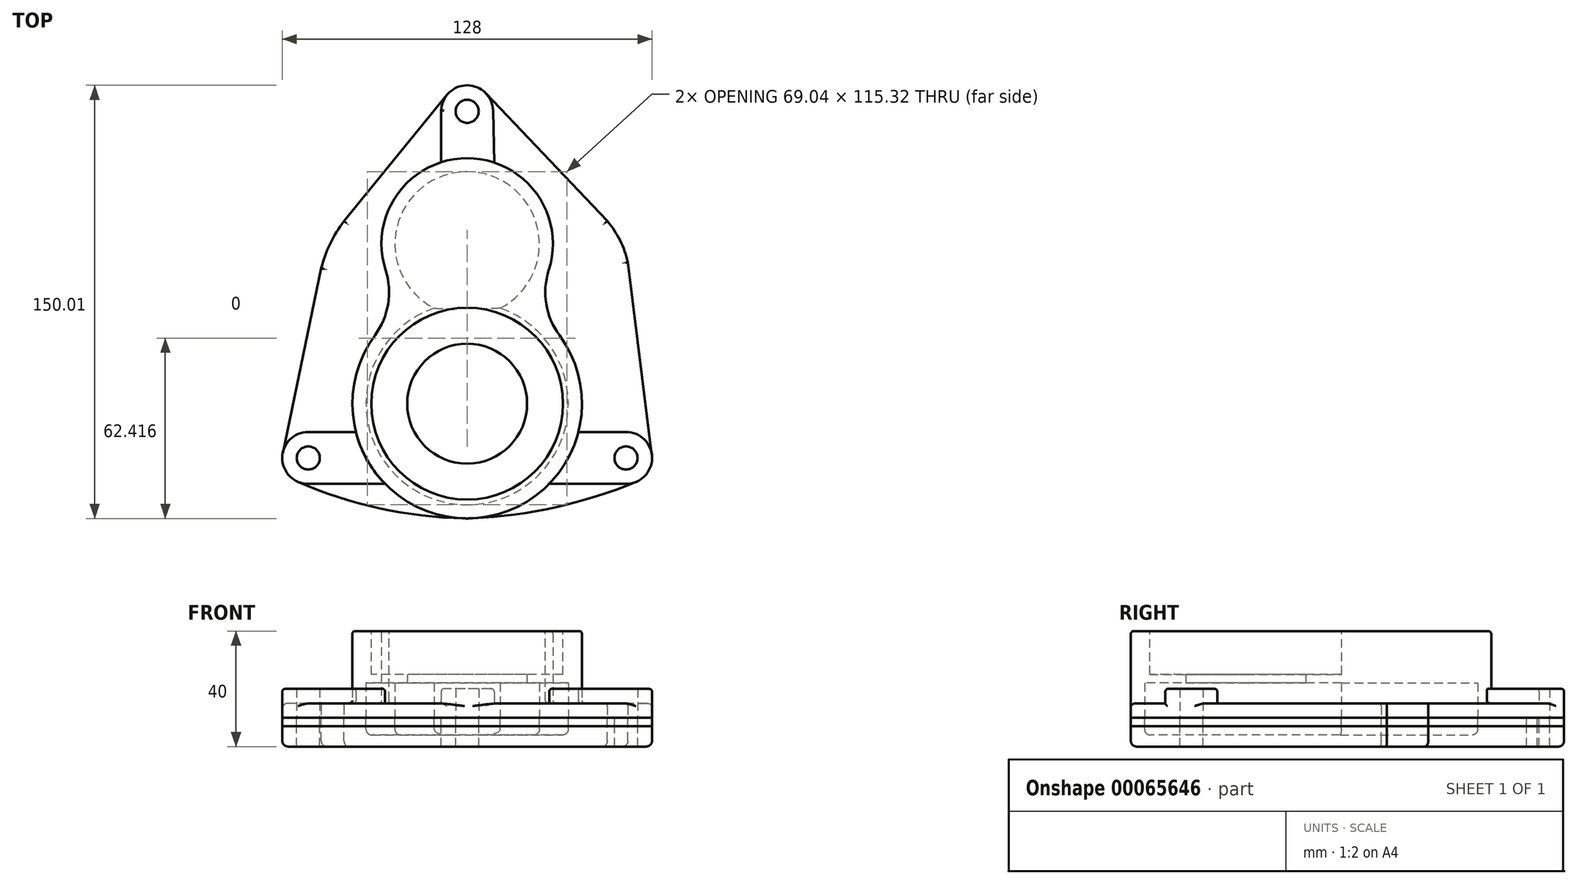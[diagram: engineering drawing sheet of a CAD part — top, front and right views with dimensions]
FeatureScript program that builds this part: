
annotation { "Feature Type Name" : "Feature", "Feature Type Description" : "" }
export const myFeature = defineFeature(function(context is Context, id is Id, definition is map)
    precondition{}
    {
        {
            var Q0;
            Q0=qCreatedBy(makeId("Top.planeOp"),FACE);
            var sketch = newSketch(context, id + "F0", { "sketchPlane" : qUnion([Q0])});
            skCircle(sketch, "E0", {"center": v(0, 23.9) * mm, "radius": 25 * mm});
            skCircle(sketch, "E1", {"center": v(0, -31.42) * mm, "radius": 20.75 * mm});
            skCircle(sketch, "E2", {"center": v(0, -31.42) * mm, "radius": 35 * mm});
            skCircle(sketch, "E3", {"center": v(0, -31.42) * mm, "radius": 39.75 * mm});
            skCircle(sketch, "E4", {"center": v(55, -50.22) * mm, "radius": 9 * mm});
            skCircle(sketch, "E5", {"center": v(-55, -50.22) * mm, "radius": 9 * mm});
            skCircle(sketch, "E6", {"center": v(0, 69.84) * mm, "radius": 9 * mm});
            skCircle(sketch, "E7", {"center": v(0, 69.84) * mm, "radius": 4 * mm});
            skCircle(sketch, "E8", {"center": v(-55, -50.22) * mm, "radius": 4 * mm});
            skCircle(sketch, "E9", {"center": v(55, -50.22) * mm, "radius": 4 * mm});
            skLineSegment(sketch, "E10", {"start": v(0, 23.9) * mm, "end": v(-25, 23.9) * mm, "construction": true});
            skLineSegment(sketch, "E11", {"start": v(0, 23.9) * mm, "end": v(25, 23.9) * mm, "construction": true});
            skLineSegment(sketch, "E12", {"start": v(-42.64, 31.8) * mm, "end": v(-6.97, 75.53) * mm});
            skLineSegment(sketch, "E13", {"start": v(48.5, 31.84) * mm, "end": v(6.53, 76.04) * mm});
            skLineSegment(sketch, "E14", {"start": v(-50.53, 15.5) * mm, "end": v(-63.81, -48.38) * mm});
            skLineSegment(sketch, "E15", {"start": v(55.66, 17.51) * mm, "end": v(63.93, -49.1) * mm});
            skArc(sketch, "E16", {"start": v(-58.6, -58.47) * mm, "mid": v(-30.36, -67.62) * mm, "end": v(-0.9, -71.16) * mm});
            skArc(sketch, "E17", {"start": v(-40.68, 34.2) * mm, "mid": v(-47.63, 23.55) * mm, "end": v(-51.38, 11.39) * mm});
            skArc(sketch, "E18", {"start": v(56.42, 11.39) * mm, "mid": v(54.21, 22.3) * mm, "end": v(48.5, 31.84) * mm});
            skPoint(sketch, "E19.orphan", {"position": v(46.26, 34.2) * mm});
            skPoint(sketch, "E20.end.orphan", {"position": v(0, -50.22) * mm});
            skLineSegment(sketch, "E21", {"start": v(-9, 70.18) * mm, "end": v(-9, 52.19) * mm});
            skLineSegment(sketch, "E22", {"start": v(9, 70.04) * mm, "end": v(9.4, 52.06) * mm});
            skArc(sketch, "E23.trimOffspring", {"start": v(20.62, 2.57) * mm, "mid": v(0.01, 53.6) * mm, "end": v(-20.62, 2.57) * mm});
            skArc(sketch, "E24", {"start": v(1.94, -71.12) * mm, "mid": v(30.72, -67.24) * mm, "end": v(58.42, -58.54) * mm});
            skLineSegment(sketch, "E25", {"start": v(-55, -41.22) * mm, "end": v(-38.53, -41.22) * mm});
            skLineSegment(sketch, "E26", {"start": v(-55, -59.22) * mm, "end": v(-28.41, -59.22) * mm});
            skLineSegment(sketch, "E27", {"start": v(55, -41.22) * mm, "end": v(38.53, -41.22) * mm});
            skLineSegment(sketch, "E28", {"start": v(55, -59.22) * mm, "end": v(28.41, -59.22) * mm});
            skCircle(sketch, "E29", {"center": v(0, -31.42) * mm, "radius": 33.2 * mm});
            skSolve(sketch);
        }
        {
            var Q0;
            {var subQ1=sQuery(id+"F0.wireOp",EDGE,"E3");var subQ3=sQuery(id+"F0.wireOp",EDGE,"E0");var subQ4=makeQuery(id+"F0.imprint","INTERSECT",VERTEX,{"disambiguationData":[OD(0.0)],"derivedFrom":[subQ3,subQ1]});Q0=makeQuery(id+"F0.imprint","IMPRINT",FACE,{"disambiguationData":[TD([[makeQuery(id+"F0.imprint","IMPRINT",EDGE,{"disambiguationData":[TD([[subQ4,1.0]])],"derivedFrom":subQ3}),-1.0]])]});}
            var Q1;
            {var subQ0=sQuery(id+"F0.wireOp",EDGE,"E3");var subQ1=sQuery(id+"F0.wireOp",EDGE,"E0");var subQ2=makeQuery(id+"F0.imprint","INTERSECT",VERTEX,{"disambiguationData":[OD(0.0)],"derivedFrom":[subQ1,subQ0]});Q1=makeQuery(id+"F0.imprint","IMPRINT",FACE,{"disambiguationData":[TD([[makeQuery(id+"F0.imprint","IMPRINT",EDGE,{"disambiguationData":[TD([[subQ2,1.0]])],"derivedFrom":subQ1}),1.0]])]});}
            var Q2;
            {var subQ0=sQuery(id+"F0.wireOp",EDGE,"E2");var subQ1=sQuery(id+"F0.wireOp",EDGE,"E0");var subQ2=makeQuery(id+"F0.imprint","INTERSECT",VERTEX,{"disambiguationData":[OD(0.0)],"derivedFrom":[subQ1,subQ0]});Q2=makeQuery(id+"F0.imprint","IMPRINT",FACE,{"disambiguationData":[TD([[makeQuery(id+"F0.imprint","IMPRINT",EDGE,{"disambiguationData":[TD([[subQ2,1.0]])],"derivedFrom":subQ1}),1.0]])]});}
            var Q3;
            {var subQ0=sQuery(id+"F0.wireOp",EDGE,"E2");var subQ1=sQuery(id+"F0.wireOp",EDGE,"E0");var subQ2=makeQuery(id+"F0.imprint","INTERSECT",VERTEX,{"disambiguationData":[OD(0.0)],"derivedFrom":[subQ1,subQ0]});Q3=makeQuery(id+"F0.imprint","IMPRINT",FACE,{"disambiguationData":[TD([[makeQuery(id+"F0.imprint","IMPRINT",EDGE,{"disambiguationData":[TD([[subQ2,-1.0]])],"derivedFrom":subQ1}),1.0]])]});}
            var Q4;
            {var subQ6=sQuery(id+"F0.wireOp",EDGE,"E2");var subQ7=sQuery(id+"F0.wireOp",EDGE,"E0");var subQ8=makeQuery(id+"F0.imprint","INTERSECT",VERTEX,{"disambiguationData":[OD(0.0)],"derivedFrom":[subQ7,subQ6]});Q4=makeQuery(id+"F0.imprint","IMPRINT",FACE,{"disambiguationData":[TD([[makeQuery(id+"F0.imprint","IMPRINT",EDGE,{"disambiguationData":[TD([[subQ8,1.0]])],"derivedFrom":subQ7}),-1.0]])]});}
            var Q5;
            Q5=makeQuery(id+"F0.imprint","IMPRINT",FACE,{"disambiguationData":[TD([[makeQuery(id+"F0.imprint","IMPRINT",EDGE,{"derivedFrom":sQuery(id+"F0.wireOp",EDGE,"E1")}),-1.0]])]});
            var Q6;
            Q6=makeQuery(id+"F0.imprint","IMPRINT",FACE,{"disambiguationData":[TD([[makeQuery(id+"F0.imprint","IMPRINT",EDGE,{"derivedFrom":sQuery(id+"F0.wireOp",EDGE,"E1")}),1.0]])]});
            var Q7;
            {var subQ0=sQuery(id+"F0.wireOp",EDGE,"E2");var subQ1=sQuery(id+"F0.wireOp",EDGE,"E0");var subQ2=makeQuery(id+"F0.imprint","INTERSECT",VERTEX,{"disambiguationData":[OD(0.0)],"derivedFrom":[subQ1,subQ0]});Q7=makeQuery(id+"F0.imprint","IMPRINT",FACE,{"disambiguationData":[TD([[makeQuery(id+"F0.imprint","IMPRINT",EDGE,{"disambiguationData":[TD([[subQ2,-1.0]])],"derivedFrom":subQ1}),-1.0]])]});}
            var Q8;
            {var subQ0=sQuery(id+"F0.wireOp",EDGE,"E29");var subQ1=sQuery(id+"F0.wireOp",EDGE,"E0");var subQ2=makeQuery(id+"F0.imprint","INTERSECT",VERTEX,{"disambiguationData":[OD(0.0)],"derivedFrom":[subQ1,subQ0]});Q8=makeQuery(id+"F0.imprint","IMPRINT",FACE,{"disambiguationData":[TD([[makeQuery(id+"F0.imprint","IMPRINT",EDGE,{"disambiguationData":[TD([[subQ2,-1.0]])],"derivedFrom":subQ1}),1.0]])]});}
            extrude(context, id + "F1", {"entities" : qUnion([Q0, Q1, Q2, Q3, Q4, Q5, Q6, Q7, Q8]), "depth" : 30 * mm});
        }
        {
            var Q0;
            {var subQ0=sQuery(id+"F0.wireOp",EDGE,"E23.trimOffspring");var subQ1=sQuery(id+"F0.wireOp",EDGE,"E3");Q0=makeQuery(id+"F1.opExtrude","SWEPT_EDGE",EDGE,{"disambiguationData":[OSD([subQ1,subQ0]),TDD([makeQuery(id+"F0.imprint","INTERSECT",VERTEX,{"disambiguationData":[OD(1.0)],"derivedFrom":[subQ1,subQ0]})])]});}
            var Q1;
            {var subQ0=sQuery(id+"F0.wireOp",EDGE,"E23.trimOffspring");var subQ1=sQuery(id+"F0.wireOp",EDGE,"E3");Q1=makeQuery(id+"F1.opExtrude","SWEPT_EDGE",EDGE,{"disambiguationData":[OSD([subQ1,subQ0]),TDD([makeQuery(id+"F0.imprint","INTERSECT",VERTEX,{"disambiguationData":[OD(0.0)],"derivedFrom":[subQ1,subQ0]})])]});}
            fillet(context, id + "F2", {"entities" : qUnion([Q0, Q1]), "radius" : 25 * mm, "tangentPropagation" : true, "allowEdgeOverflow" : false});
        }
        {
            var Q0;
            Q0=makeQuery(id+"F0.imprint","IMPRINT",FACE,{"disambiguationData":[TD([[makeQuery(id+"F0.imprint","IMPRINT",EDGE,{"derivedFrom":sQuery(id+"F0.wireOp",EDGE,"E7")}),-1.0]])]});
            var Q1;
            {var subQ0=sQuery(id+"F0.wireOp",EDGE,"E22");var subQ1=sQuery(id+"F0.wireOp",EDGE,"E6");var subQ2=makeQuery(id+"F0.imprint","INTERSECT",VERTEX,{"derivedFrom":[subQ1,subQ0]});Q1=makeQuery(id+"F0.imprint","IMPRINT",FACE,{"disambiguationData":[TD([[makeQuery(id+"F0.imprint","IMPRINT",EDGE,{"disambiguationData":[TD([[subQ2,1.0]])],"derivedFrom":subQ1}),-1.0]])]});}
            var Q2;
            {var subQ0=sQuery(id+"F0.wireOp",EDGE,"E25");Q2=makeQuery(id+"F0.imprint","IMPRINT",FACE,{"disambiguationData":[TD([[makeQuery(id+"F0.imprint","IMPRINT",EDGE,{"derivedFrom":subQ0}),-1.0]])]});}
            var Q3;
            Q3=makeQuery(id+"F0.imprint","IMPRINT",FACE,{"disambiguationData":[TD([[makeQuery(id+"F0.imprint","IMPRINT",EDGE,{"derivedFrom":sQuery(id+"F0.wireOp",EDGE,"E8")}),-1.0]])]});
            var Q4;
            {var subQ0=sQuery(id+"F0.wireOp",EDGE,"E27");Q4=makeQuery(id+"F0.imprint","IMPRINT",FACE,{"disambiguationData":[TD([[makeQuery(id+"F0.imprint","IMPRINT",EDGE,{"derivedFrom":subQ0}),1.0]])]});}
            var Q5;
            Q5=makeQuery(id+"F0.imprint","IMPRINT",FACE,{"disambiguationData":[TD([[makeQuery(id+"F0.imprint","IMPRINT",EDGE,{"derivedFrom":sQuery(id+"F0.wireOp",EDGE,"E9")}),-1.0]])]});
            extrude(context, id + "F3", {"entities" : qUnion([Q0, Q1, Q2, Q3, Q4, Q5]), "operationType" : NewBodyOperationType.ADD, "depth" : 10 * mm});
        }
        {
            var Q0;
            {var subQ18=sQuery(id+"F0.wireOp",EDGE,"E25");Q0=makeQuery(id+"F0.imprint","IMPRINT",FACE,{"disambiguationData":[TD([[makeQuery(id+"F0.imprint","IMPRINT",EDGE,{"derivedFrom":subQ18}),1.0]])]});}
            var Q1;
            {var subQ0=sQuery(id+"F0.wireOp",EDGE,"E13");Q1=makeQuery(id+"F0.imprint","IMPRINT",FACE,{"disambiguationData":[TD([[makeQuery(id+"F0.imprint","IMPRINT",EDGE,{"derivedFrom":subQ0}),1.0]])]});}
            var Q2;
            {var subQ0=sQuery(id+"F0.wireOp",EDGE,"E24");Q2=makeQuery(id+"F0.imprint","IMPRINT",FACE,{"disambiguationData":[TD([[makeQuery(id+"F0.imprint","IMPRINT",EDGE,{"derivedFrom":subQ0}),1.0]])]});}
            var Q3;
            {var subQ0=sQuery(id+"F0.wireOp",EDGE,"E16");Q3=makeQuery(id+"F0.imprint","IMPRINT",FACE,{"disambiguationData":[TD([[makeQuery(id+"F0.imprint","IMPRINT",EDGE,{"derivedFrom":subQ0}),1.0]])]});}
            extrude(context, id + "F4", {"entities" : qUnion([Q0, Q1, Q2, Q3]), "operationType" : NewBodyOperationType.ADD, "depth" : 5 * mm});
        }
        {
            var Q0;
            {var subQ0=sQuery(id+"F0.wireOp",EDGE,"E3");var subQ1=sQuery(id+"F0.wireOp",EDGE,"E0");var subQ2=makeQuery(id+"F0.imprint","INTERSECT",VERTEX,{"disambiguationData":[OD(0.0)],"derivedFrom":[subQ1,subQ0]});Q0=makeQuery(id+"F0.imprint","IMPRINT",FACE,{"disambiguationData":[TD([[makeQuery(id+"F0.imprint","IMPRINT",EDGE,{"disambiguationData":[TD([[subQ2,1.0]])],"derivedFrom":subQ1}),1.0]])]});}
            var Q1;
            {var subQ0=sQuery(id+"F0.wireOp",EDGE,"E2");var subQ1=sQuery(id+"F0.wireOp",EDGE,"E0");var subQ2=makeQuery(id+"F0.imprint","INTERSECT",VERTEX,{"disambiguationData":[OD(0.0)],"derivedFrom":[subQ1,subQ0]});Q1=makeQuery(id+"F0.imprint","IMPRINT",FACE,{"disambiguationData":[TD([[makeQuery(id+"F0.imprint","IMPRINT",EDGE,{"disambiguationData":[TD([[subQ2,1.0]])],"derivedFrom":subQ1}),1.0]])]});}
            var Q2;
            {var subQ0=sQuery(id+"F0.wireOp",EDGE,"E2");var subQ1=sQuery(id+"F0.wireOp",EDGE,"E0");var subQ2=makeQuery(id+"F0.imprint","INTERSECT",VERTEX,{"disambiguationData":[OD(0.0)],"derivedFrom":[subQ1,subQ0]});Q2=makeQuery(id+"F0.imprint","IMPRINT",FACE,{"disambiguationData":[TD([[makeQuery(id+"F0.imprint","IMPRINT",EDGE,{"disambiguationData":[TD([[subQ2,-1.0]])],"derivedFrom":subQ1}),1.0]])]});}
            var Q3;
            {var subQ0=sQuery(id+"F0.wireOp",EDGE,"E29");var subQ1=sQuery(id+"F0.wireOp",EDGE,"E0");var subQ2=makeQuery(id+"F0.imprint","INTERSECT",VERTEX,{"disambiguationData":[OD(0.0)],"derivedFrom":[subQ1,subQ0]});Q3=makeQuery(id+"F0.imprint","IMPRINT",FACE,{"disambiguationData":[TD([[makeQuery(id+"F0.imprint","IMPRINT",EDGE,{"disambiguationData":[TD([[subQ2,-1.0]])],"derivedFrom":subQ1}),1.0]])]});}
            var Q4;
            Q4=makeQuery(id+"F0.imprint","IMPRINT",FACE,{"disambiguationData":[TD([[makeQuery(id+"F0.imprint","IMPRINT",EDGE,{"derivedFrom":sQuery(id+"F0.wireOp",EDGE,"E1")}),-1.0]])]});
            var Q5;
            Q5=makeQuery(id+"F0.imprint","IMPRINT",FACE,{"disambiguationData":[TD([[makeQuery(id+"F0.imprint","IMPRINT",EDGE,{"derivedFrom":sQuery(id+"F0.wireOp",EDGE,"E1")}),1.0]])]});
            var Q6;
            {var subQ0=sQuery(id+"F0.wireOp",EDGE,"E2");var subQ1=sQuery(id+"F0.wireOp",EDGE,"E0");var subQ2=makeQuery(id+"F0.imprint","INTERSECT",VERTEX,{"disambiguationData":[OD(0.0)],"derivedFrom":[subQ1,subQ0]});Q6=makeQuery(id+"F0.imprint","IMPRINT",FACE,{"disambiguationData":[TD([[makeQuery(id+"F0.imprint","IMPRINT",EDGE,{"disambiguationData":[TD([[subQ2,-1.0]])],"derivedFrom":subQ1}),-1.0]])]});}
            extrude(context, id + "F5", {"entities" : qUnion([Q0, Q1, Q2, Q3, Q4, Q5, Q6]), "operationType" : NewBodyOperationType.REMOVE, "depth" : 12 * mm});
        }
        {
            var Q0;
            Q0=makeQuery(id+"F1.opExtrude","CAP_FACE",FACE,{"disambiguationData":[OSD([sQuery(id+"F0.wireOp",EDGE,"E3"),sQuery(id+"F0.wireOp",EDGE,"E23.trimOffspring")])],"isStart":false});
            var sketch = newSketch(context, id + "F6", { "sketchPlane" : qUnion([Q0])});
            skCircle(sketch, "E30.0", {"center": v(0, -31.42) * mm, "radius": 33.2 * mm});
            skCircle(sketch, "E31.0", {"center": v(0, 23.9) * mm, "radius": 25 * mm});
            skSolve(sketch);
        }
        {
            var Q0;
            Q0=makeQuery(id+"F6.imprint","IMPRINT",FACE,{"disambiguationData":[TD([[makeQuery(id+"F6.imprint","IMPRINT",EDGE,{"derivedFrom":sQuery(id+"F6.wireOp",EDGE,"E30.0")}),1.0]])]});
            extrude(context, id + "F7", {"entities" : qUnion([Q0]), "operationType" : NewBodyOperationType.REMOVE, "oppositeDirection" : true, "depth" : 15 * mm});
        }
        {
            var Q0;
            Q0=makeQuery(id+"F0.imprint","IMPRINT",FACE,{"disambiguationData":[TD([[makeQuery(id+"F0.imprint","IMPRINT",EDGE,{"derivedFrom":sQuery(id+"F0.wireOp",EDGE,"E1")}),1.0]])]});
            extrude(context, id + "F8", {"entities" : qUnion([Q0]), "operationType" : NewBodyOperationType.REMOVE, "endBound" : BoundingType.THROUGH_ALL, "depth" : 25 * mm});
        }
        {
            var Q0;
            Q0=makeQuery(id+"F1.opExtrude","CAP_EDGE",EDGE,{"disambiguationData":[OSD([sQuery(id+"F0.wireOp",EDGE,"E3")])],"isStart":false});
            var Q1;
            {var subQ0=sQuery(id+"F0.wireOp",EDGE,"E23.trimOffspring");var subQ1=sQuery(id+"F0.wireOp",EDGE,"E3");Q1=makeQuery(id+"F2.opFillet","BLEND_EDGE",EDGE,{"blendedFrom":[makeQuery(id+"F1.opExtrude","SWEPT_EDGE",EDGE,{"disambiguationData":[OSD([subQ1,subQ0]),TDD([makeQuery(id+"F0.imprint","INTERSECT",VERTEX,{"disambiguationData":[OD(0.0)],"derivedFrom":[subQ1,subQ0]})])]}),makeQuery(id+"F1.opExtrude","CAP_FACE",FACE,{"disambiguationData":[OSD([subQ1,subQ0])],"isStart":false})],"blendedInto":[makeQuery(id+"F1.opExtrude","CAP_FACE",FACE,{"disambiguationData":[OSD([subQ1,subQ0])],"isStart":false})]});}
            var Q2;
            Q2=makeQuery(id+"F1.opExtrude","CAP_EDGE",EDGE,{"disambiguationData":[OSD([sQuery(id+"F0.wireOp",EDGE,"E23.trimOffspring")])],"isStart":false});
            var Q3;
            {var subQ0=sQuery(id+"F0.wireOp",EDGE,"E23.trimOffspring");var subQ1=sQuery(id+"F0.wireOp",EDGE,"E3");Q3=makeQuery(id+"F4.boolean.opBoolean","INTERSECT",EDGE,{"derivedFrom":[makeQuery(id+"F2.opFillet","BLEND_FACE",FACE,{"disambiguationData":[OSD([subQ1,subQ0]),TDD([makeQuery(id+"F1.opExtrude","SWEPT_EDGE",EDGE,{"disambiguationData":[OSD([subQ1,subQ0]),TDD([makeQuery(id+"F0.imprint","INTERSECT",VERTEX,{"disambiguationData":[OD(0.0)],"derivedFrom":[subQ1,subQ0]})])]})])]}),makeQuery(id+"F4.opExtrude","CAP_FACE",FACE,{"disambiguationData":[OSD([subQ1,sQuery(id+"F0.wireOp",EDGE,"E4"),sQuery(id+"F0.wireOp",EDGE,"E6"),sQuery(id+"F0.wireOp",EDGE,"E13"),sQuery(id+"F0.wireOp",EDGE,"E15"),sQuery(id+"F0.wireOp",EDGE,"E18"),sQuery(id+"F0.wireOp",EDGE,"E22"),subQ0,sQuery(id+"F0.wireOp",EDGE,"E27")])],"isStart":false})]});}
            var Q4;
            {var subQ0=sQuery(id+"F0.wireOp",EDGE,"E3");Q4=makeQuery(id+"F4.opExtrude","CAP_EDGE",EDGE,{"disambiguationData":[OSD([subQ0]),TDD([makeQuery(id+"F0.imprint","IMPRINT",EDGE,{"disambiguationData":[TD([[makeQuery(id+"F0.imprint","INTERSECT",VERTEX,{"derivedFrom":[subQ0,sQuery(id+"F0.wireOp",EDGE,"E24")]}),-1.0]])],"derivedFrom":subQ0})])],"isStart":false});}
            var Q5;
            Q5=makeQuery(id+"F3.opExtrude","SWEPT_EDGE",EDGE,{"disambiguationData":[OSD([sQuery(id+"F0.wireOp",EDGE,"E3"),sQuery(id+"F0.wireOp",EDGE,"E28")])]});
            var Q6;
            {var subQ0=sQuery(id+"F0.wireOp",EDGE,"E3");Q6=makeQuery(id+"F3.opExtrude","CAP_EDGE",EDGE,{"disambiguationData":[OSD([subQ0]),TDD([makeQuery(id+"F0.imprint","IMPRINT",EDGE,{"disambiguationData":[TD([[makeQuery(id+"F0.imprint","INTERSECT",VERTEX,{"derivedFrom":[subQ0,sQuery(id+"F0.wireOp",EDGE,"E27")]}),1.0]])],"derivedFrom":subQ0})])],"isStart":false});}
            var Q7;
            Q7=makeQuery(id+"F3.opExtrude","CAP_EDGE",EDGE,{"disambiguationData":[OSD([sQuery(id+"F0.wireOp",EDGE,"E28")])],"isStart":false});
            var Q8;
            Q8=makeQuery(id+"F4.opExtrude","CAP_EDGE",EDGE,{"disambiguationData":[OSD([sQuery(id+"F0.wireOp",EDGE,"E28")])],"isStart":false});
            var Q9;
            Q9=makeQuery(id+"F4.opExtrude","CAP_EDGE",EDGE,{"disambiguationData":[OSD([sQuery(id+"F0.wireOp",EDGE,"E24")])],"isStart":false});
            var Q10;
            Q10=makeQuery(id+"F4.opExtrude","CAP_EDGE",EDGE,{"disambiguationData":[OSD([sQuery(id+"F0.wireOp",EDGE,"E15")])],"isStart":false});
            var Q11;
            Q11=makeQuery(id+"F4.opExtrude","CAP_EDGE",EDGE,{"disambiguationData":[OSD([sQuery(id+"F0.wireOp",EDGE,"E18")])],"isStart":false});
            var Q12;
            Q12=makeQuery(id+"F3.opExtrude","CAP_EDGE",EDGE,{"disambiguationData":[OSD([sQuery(id+"F0.wireOp",EDGE,"E22")])],"isStart":false});
            var Q13;
            Q13=makeQuery(id+"F3.opExtrude","CAP_EDGE",EDGE,{"disambiguationData":[OSD([sQuery(id+"F0.wireOp",EDGE,"E23.trimOffspring")])],"isStart":false});
            var Q14;
            {var subQ0=sQuery(id+"F0.wireOp",EDGE,"E23.trimOffspring");Q14=makeQuery(id+"F4.opExtrude","CAP_EDGE",EDGE,{"disambiguationData":[OSD([subQ0]),TDD([makeQuery(id+"F0.imprint","IMPRINT",EDGE,{"disambiguationData":[TD([[makeQuery(id+"F0.imprint","INTERSECT",VERTEX,{"disambiguationData":[OD(0.0)],"derivedFrom":[sQuery(id+"F0.wireOp",EDGE,"E3"),subQ0]}),-1.0]])],"derivedFrom":subQ0})])],"isStart":false});}
            var Q15;
            {var subQ0=sQuery(id+"F0.wireOp",EDGE,"E3");Q15=makeQuery(id+"F4.opExtrude","CAP_EDGE",EDGE,{"disambiguationData":[OSD([subQ0]),TDD([makeQuery(id+"F0.imprint","IMPRINT",EDGE,{"disambiguationData":[TD([[makeQuery(id+"F0.imprint","INTERSECT",VERTEX,{"disambiguationData":[OD(0.0)],"derivedFrom":[subQ0,sQuery(id+"F0.wireOp",EDGE,"E23.trimOffspring")]}),1.0]])],"derivedFrom":subQ0})])],"isStart":false});}
            var Q16;
            Q16=makeQuery(id+"F3.opExtrude","SWEPT_EDGE",EDGE,{"disambiguationData":[OSD([sQuery(id+"F0.wireOp",EDGE,"E3"),sQuery(id+"F0.wireOp",EDGE,"E27")])]});
            var Q17;
            Q17=makeQuery(id+"F4.opExtrude","CAP_EDGE",EDGE,{"disambiguationData":[OSD([sQuery(id+"F0.wireOp",EDGE,"E27")])],"isStart":false});
            var Q18;
            Q18=makeQuery(id+"F3.opExtrude","CAP_EDGE",EDGE,{"disambiguationData":[OSD([sQuery(id+"F0.wireOp",EDGE,"E27")])],"isStart":false});
            var Q19;
            Q19=makeQuery(id+"F3.opExtrude","CAP_EDGE",EDGE,{"disambiguationData":[OSD([sQuery(id+"F0.wireOp",EDGE,"E4")])],"isStart":false});
            var Q20;
            {var subQ0=sQuery(id+"F0.wireOp",EDGE,"E4");Q20=makeQuery(id+"F4.opExtrude","CAP_EDGE",EDGE,{"disambiguationData":[OSD([subQ0]),TDD([makeQuery(id+"F0.imprint","IMPRINT",EDGE,{"disambiguationData":[TD([[makeQuery(id+"F0.imprint","INTERSECT",VERTEX,{"derivedFrom":[subQ0,sQuery(id+"F0.wireOp",EDGE,"E15")]}),-1.0]])],"derivedFrom":subQ0})])],"isStart":false});}
            var Q21;
            Q21=makeQuery(id+"F4.opExtrude","CAP_EDGE",EDGE,{"disambiguationData":[OSD([sQuery(id+"F0.wireOp",EDGE,"E13")])],"isStart":false});
            var Q22;
            Q22=makeQuery(id+"F3.opExtrude","CAP_EDGE",EDGE,{"disambiguationData":[OSD([sQuery(id+"F0.wireOp",EDGE,"E6")])],"isStart":false});
            var Q23;
            Q23=makeQuery(id+"F3.opExtrude","CAP_EDGE",EDGE,{"disambiguationData":[OSD([sQuery(id+"F0.wireOp",EDGE,"E21")])],"isStart":false});
            var Q24;
            {var subQ0=sQuery(id+"F0.wireOp",EDGE,"E23.trimOffspring");Q24=makeQuery(id+"F4.opExtrude","CAP_EDGE",EDGE,{"disambiguationData":[OSD([subQ0]),TDD([makeQuery(id+"F0.imprint","IMPRINT",EDGE,{"disambiguationData":[TD([[makeQuery(id+"F0.imprint","INTERSECT",VERTEX,{"disambiguationData":[OD(1.0)],"derivedFrom":[sQuery(id+"F0.wireOp",EDGE,"E3"),subQ0]}),1.0]])],"derivedFrom":subQ0})])],"isStart":false});}
            var Q25;
            {var subQ0=sQuery(id+"F0.wireOp",EDGE,"E23.trimOffspring");var subQ1=sQuery(id+"F0.wireOp",EDGE,"E3");Q25=makeQuery(id+"F4.boolean.opBoolean","INTERSECT",EDGE,{"derivedFrom":[makeQuery(id+"F2.opFillet","BLEND_FACE",FACE,{"disambiguationData":[OSD([subQ1,subQ0]),TDD([makeQuery(id+"F1.opExtrude","SWEPT_EDGE",EDGE,{"disambiguationData":[OSD([subQ1,subQ0]),TDD([makeQuery(id+"F0.imprint","INTERSECT",VERTEX,{"disambiguationData":[OD(1.0)],"derivedFrom":[subQ1,subQ0]})])]})])]}),makeQuery(id+"F4.opExtrude","CAP_FACE",FACE,{"disambiguationData":[OSD([subQ1,sQuery(id+"F0.wireOp",EDGE,"E5"),sQuery(id+"F0.wireOp",EDGE,"E6"),sQuery(id+"F0.wireOp",EDGE,"E12"),sQuery(id+"F0.wireOp",EDGE,"E14"),sQuery(id+"F0.wireOp",EDGE,"E17"),sQuery(id+"F0.wireOp",EDGE,"E21"),subQ0,sQuery(id+"F0.wireOp",EDGE,"E25")])],"isStart":false})]});}
            var Q26;
            Q26=makeQuery(id+"F4.opExtrude","CAP_EDGE",EDGE,{"disambiguationData":[OSD([sQuery(id+"F0.wireOp",EDGE,"E17")])],"isStart":false});
            var Q27;
            {var subQ0=sQuery(id+"F0.wireOp",EDGE,"E21");var subQ1=sQuery(id+"F0.wireOp",EDGE,"E6");var subQ2=makeQuery(id+"F0.imprint","INTERSECT",VERTEX,{"disambiguationData":[OD(0.0)],"derivedFrom":[subQ1,subQ0]});Q27=makeQuery(id+"F4.boolean.opBoolean","MERGE",EDGE,{"derivedFrom":[makeQuery(id+"F4.opExtrude","CAP_EDGE",EDGE,{"disambiguationData":[OSD([subQ1]),TDD([makeQuery(id+"F0.imprint","IMPRINT",EDGE,{"disambiguationData":[TD([[makeQuery(id+"F0.imprint","INTERSECT",VERTEX,{"derivedFrom":[subQ1,sQuery(id+"F0.wireOp",EDGE,"E12")]}),-1.0]])],"derivedFrom":subQ1}),makeQuery(id+"F0.imprint","IMPRINT",EDGE,{"disambiguationData":[TD([[subQ2,-1.0]])],"derivedFrom":subQ1})])],"isStart":false}),makeQuery(id+"F4.opExtrude","CAP_EDGE",EDGE,{"disambiguationData":[OSD([subQ0])],"isStart":false})]});}
            var Q28;
            {var subQ0=sQuery(id+"F0.wireOp",EDGE,"E21");var subQ1=sQuery(id+"F0.wireOp",EDGE,"E6");var subQ2=makeQuery(id+"F0.imprint","INTERSECT",VERTEX,{"disambiguationData":[OD(0.0)],"derivedFrom":[subQ1,subQ0]});Q28=makeQuery(id+"F4.boolean.opBoolean","SPLIT",EDGE,{"derivedFrom":makeQuery(id+"F4.opExtrude","CAP_EDGE",EDGE,{"disambiguationData":[OSD([subQ1]),TDD([makeQuery(id+"F0.imprint","IMPRINT",EDGE,{"disambiguationData":[TD([[makeQuery(id+"F0.imprint","INTERSECT",VERTEX,{"derivedFrom":[subQ1,sQuery(id+"F0.wireOp",EDGE,"E12")]}),-1.0]])],"derivedFrom":subQ1}),makeQuery(id+"F0.imprint","IMPRINT",EDGE,{"disambiguationData":[TD([[subQ2,-1.0]])],"derivedFrom":subQ1})])],"isStart":false})});}
            var Q29;
            Q29=makeQuery(id+"F4.opExtrude","CAP_EDGE",EDGE,{"disambiguationData":[OSD([sQuery(id+"F0.wireOp",EDGE,"E12")])],"isStart":false});
            var Q30;
            Q30=makeQuery(id+"F4.opExtrude","CAP_EDGE",EDGE,{"disambiguationData":[OSD([sQuery(id+"F0.wireOp",EDGE,"E25")])],"isStart":false});
            var Q31;
            {var subQ0=sQuery(id+"F0.wireOp",EDGE,"E5");Q31=makeQuery(id+"F4.opExtrude","CAP_EDGE",EDGE,{"disambiguationData":[OSD([subQ0]),TDD([makeQuery(id+"F0.imprint","IMPRINT",EDGE,{"disambiguationData":[TD([[makeQuery(id+"F0.imprint","INTERSECT",VERTEX,{"derivedFrom":[subQ0,sQuery(id+"F0.wireOp",EDGE,"E14")]}),1.0]])],"derivedFrom":subQ0})])],"isStart":false});}
            var Q32;
            Q32=makeQuery(id+"F4.opExtrude","CAP_EDGE",EDGE,{"disambiguationData":[OSD([sQuery(id+"F0.wireOp",EDGE,"E14")])],"isStart":false});
            var Q33;
            Q33=makeQuery(id+"F3.opExtrude","CAP_EDGE",EDGE,{"disambiguationData":[OSD([sQuery(id+"F0.wireOp",EDGE,"E25")])],"isStart":false});
            var Q34;
            {var subQ0=sQuery(id+"F0.wireOp",EDGE,"E3");Q34=makeQuery(id+"F3.opExtrude","CAP_EDGE",EDGE,{"disambiguationData":[OSD([subQ0]),TDD([makeQuery(id+"F0.imprint","IMPRINT",EDGE,{"disambiguationData":[TD([[makeQuery(id+"F0.imprint","INTERSECT",VERTEX,{"derivedFrom":[subQ0,sQuery(id+"F0.wireOp",EDGE,"E25")]}),-1.0]])],"derivedFrom":subQ0})])],"isStart":false});}
            var Q35;
            {var subQ0=sQuery(id+"F0.wireOp",EDGE,"E23.trimOffspring");var subQ1=sQuery(id+"F0.wireOp",EDGE,"E3");Q35=makeQuery(id+"F2.opFillet","BLEND_EDGE",EDGE,{"blendedFrom":[makeQuery(id+"F1.opExtrude","SWEPT_EDGE",EDGE,{"disambiguationData":[OSD([subQ1,subQ0]),TDD([makeQuery(id+"F0.imprint","INTERSECT",VERTEX,{"disambiguationData":[OD(1.0)],"derivedFrom":[subQ1,subQ0]})])]}),makeQuery(id+"F1.opExtrude","CAP_FACE",FACE,{"disambiguationData":[OSD([subQ1,subQ0])],"isStart":false})],"blendedInto":[makeQuery(id+"F1.opExtrude","CAP_FACE",FACE,{"disambiguationData":[OSD([subQ1,subQ0])],"isStart":false})]});}
            var Q36;
            Q36=makeQuery(id+"F4.opExtrude","CAP_EDGE",EDGE,{"disambiguationData":[OSD([sQuery(id+"F0.wireOp",EDGE,"E26")])],"isStart":false});
            var Q37;
            Q37=makeQuery(id+"F4.opExtrude","CAP_EDGE",EDGE,{"disambiguationData":[OSD([sQuery(id+"F0.wireOp",EDGE,"E16")])],"isStart":false});
            var Q38;
            {var subQ0=sQuery(id+"F0.wireOp",EDGE,"E3");Q38=makeQuery(id+"F4.opExtrude","CAP_EDGE",EDGE,{"disambiguationData":[OSD([subQ0]),TDD([makeQuery(id+"F0.imprint","IMPRINT",EDGE,{"disambiguationData":[TD([[makeQuery(id+"F0.imprint","INTERSECT",VERTEX,{"derivedFrom":[subQ0,sQuery(id+"F0.wireOp",EDGE,"E16")]}),1.0]])],"derivedFrom":subQ0})])],"isStart":false});}
            fillet(context, id + "F9", {"entities" : qUnion([Q0, Q1, Q2, Q3, Q4, Q5, Q6, Q7, Q8, Q9, Q10, Q11, Q12, Q13, Q14, Q15, Q16, Q17, Q18, Q19, Q20, Q21, Q22, Q23, Q24, Q25, Q26, Q27, Q28, Q29, Q30, Q31, Q32, Q33, Q34, Q35, Q36, Q37, Q38]), "radius" : 1 * mm, "tangentPropagation" : true, "allowEdgeOverflow" : false});
        }
        {
            var Q0;
            {var subQ18=sQuery(id+"F0.wireOp",EDGE,"E25");Q0=makeQuery(id+"F0.imprint","IMPRINT",FACE,{"disambiguationData":[TD([[makeQuery(id+"F0.imprint","IMPRINT",EDGE,{"derivedFrom":subQ18}),1.0]])]});}
            var Q1;
            Q1=makeQuery(id+"F0.imprint","IMPRINT",FACE,{"disambiguationData":[TD([[makeQuery(id+"F0.imprint","IMPRINT",EDGE,{"derivedFrom":sQuery(id+"F0.wireOp",EDGE,"E8")}),-1.0]])]});
            var Q2;
            {var subQ0=sQuery(id+"F0.wireOp",EDGE,"E25");Q2=makeQuery(id+"F0.imprint","IMPRINT",FACE,{"disambiguationData":[TD([[makeQuery(id+"F0.imprint","IMPRINT",EDGE,{"derivedFrom":subQ0}),-1.0]])]});}
            var Q3;
            {var subQ0=sQuery(id+"F0.wireOp",EDGE,"E16");Q3=makeQuery(id+"F0.imprint","IMPRINT",FACE,{"disambiguationData":[TD([[makeQuery(id+"F0.imprint","IMPRINT",EDGE,{"derivedFrom":subQ0}),1.0]])]});}
            var Q4;
            {var subQ3=sQuery(id+"F0.wireOp",EDGE,"E2");var subQ4=sQuery(id+"F0.wireOp",EDGE,"E0");var subQ5=makeQuery(id+"F0.imprint","INTERSECT",VERTEX,{"disambiguationData":[OD(0.0)],"derivedFrom":[subQ4,subQ3]});Q4=makeQuery(id+"F0.imprint","IMPRINT",FACE,{"disambiguationData":[TD([[makeQuery(id+"F0.imprint","IMPRINT",EDGE,{"disambiguationData":[TD([[subQ5,1.0]])],"derivedFrom":subQ4}),-1.0]])]});}
            var Q5;
            {var subQ0=sQuery(id+"F0.wireOp",EDGE,"E24");Q5=makeQuery(id+"F0.imprint","IMPRINT",FACE,{"disambiguationData":[TD([[makeQuery(id+"F0.imprint","IMPRINT",EDGE,{"derivedFrom":subQ0}),1.0]])]});}
            var Q6;
            {var subQ0=sQuery(id+"F0.wireOp",EDGE,"E27");Q6=makeQuery(id+"F0.imprint","IMPRINT",FACE,{"disambiguationData":[TD([[makeQuery(id+"F0.imprint","IMPRINT",EDGE,{"derivedFrom":subQ0}),1.0]])]});}
            var Q7;
            Q7=makeQuery(id+"F0.imprint","IMPRINT",FACE,{"disambiguationData":[TD([[makeQuery(id+"F0.imprint","IMPRINT",EDGE,{"derivedFrom":sQuery(id+"F0.wireOp",EDGE,"E9")}),-1.0]])]});
            var Q8;
            {var subQ1=sQuery(id+"F0.wireOp",EDGE,"E3");var subQ3=sQuery(id+"F0.wireOp",EDGE,"E0");var subQ4=makeQuery(id+"F0.imprint","INTERSECT",VERTEX,{"disambiguationData":[OD(0.0)],"derivedFrom":[subQ3,subQ1]});Q8=makeQuery(id+"F0.imprint","IMPRINT",FACE,{"disambiguationData":[TD([[makeQuery(id+"F0.imprint","IMPRINT",EDGE,{"disambiguationData":[TD([[subQ4,1.0]])],"derivedFrom":subQ3}),-1.0]])]});}
            var Q9;
            {var subQ0=sQuery(id+"F0.wireOp",EDGE,"E22");var subQ1=sQuery(id+"F0.wireOp",EDGE,"E6");var subQ2=makeQuery(id+"F0.imprint","INTERSECT",VERTEX,{"derivedFrom":[subQ1,subQ0]});Q9=makeQuery(id+"F0.imprint","IMPRINT",FACE,{"disambiguationData":[TD([[makeQuery(id+"F0.imprint","IMPRINT",EDGE,{"disambiguationData":[TD([[subQ2,1.0]])],"derivedFrom":subQ1}),-1.0]])]});}
            var Q10;
            Q10=makeQuery(id+"F0.imprint","IMPRINT",FACE,{"disambiguationData":[TD([[makeQuery(id+"F0.imprint","IMPRINT",EDGE,{"derivedFrom":sQuery(id+"F0.wireOp",EDGE,"E7")}),-1.0]])]});
            var Q11;
            {var subQ0=sQuery(id+"F0.wireOp",EDGE,"E13");Q11=makeQuery(id+"F0.imprint","IMPRINT",FACE,{"disambiguationData":[TD([[makeQuery(id+"F0.imprint","IMPRINT",EDGE,{"derivedFrom":subQ0}),1.0]])]});}
            extrude(context, id + "F10", {"entities" : qUnion([Q0, Q1, Q2, Q3, Q4, Q5, Q6, Q7, Q8, Q9, Q10, Q11]), "oppositeDirection" : true, "depth" : 3 * mm});
        }
        {
            var Q0;
            {var subQ0=sQuery(id+"F0.wireOp",EDGE,"E3");var subQ1=sQuery(id+"F0.wireOp",EDGE,"E0");var subQ2=makeQuery(id+"F0.imprint","INTERSECT",VERTEX,{"disambiguationData":[OD(0.0)],"derivedFrom":[subQ1,subQ0]});Q0=makeQuery(id+"F0.imprint","IMPRINT",FACE,{"disambiguationData":[TD([[makeQuery(id+"F0.imprint","IMPRINT",EDGE,{"disambiguationData":[TD([[subQ2,1.0]])],"derivedFrom":subQ1}),1.0]])]});}
            var Q1;
            {var subQ1=sQuery(id+"F0.wireOp",EDGE,"E3");var subQ3=sQuery(id+"F0.wireOp",EDGE,"E0");var subQ4=makeQuery(id+"F0.imprint","INTERSECT",VERTEX,{"disambiguationData":[OD(0.0)],"derivedFrom":[subQ3,subQ1]});Q1=makeQuery(id+"F0.imprint","IMPRINT",FACE,{"disambiguationData":[TD([[makeQuery(id+"F0.imprint","IMPRINT",EDGE,{"disambiguationData":[TD([[subQ4,1.0]])],"derivedFrom":subQ3}),-1.0]])]});}
            var Q2;
            {var subQ0=sQuery(id+"F0.wireOp",EDGE,"E2");var subQ1=sQuery(id+"F0.wireOp",EDGE,"E0");var subQ2=makeQuery(id+"F0.imprint","INTERSECT",VERTEX,{"disambiguationData":[OD(0.0)],"derivedFrom":[subQ1,subQ0]});Q2=makeQuery(id+"F0.imprint","IMPRINT",FACE,{"disambiguationData":[TD([[makeQuery(id+"F0.imprint","IMPRINT",EDGE,{"disambiguationData":[TD([[subQ2,1.0]])],"derivedFrom":subQ1}),1.0]])]});}
            var Q3;
            {var subQ3=sQuery(id+"F0.wireOp",EDGE,"E2");var subQ4=sQuery(id+"F0.wireOp",EDGE,"E0");var subQ5=makeQuery(id+"F0.imprint","INTERSECT",VERTEX,{"disambiguationData":[OD(0.0)],"derivedFrom":[subQ4,subQ3]});Q3=makeQuery(id+"F0.imprint","IMPRINT",FACE,{"disambiguationData":[TD([[makeQuery(id+"F0.imprint","IMPRINT",EDGE,{"disambiguationData":[TD([[subQ5,1.0]])],"derivedFrom":subQ4}),-1.0]])]});}
            var Q4;
            {var subQ18=sQuery(id+"F0.wireOp",EDGE,"E25");Q4=makeQuery(id+"F0.imprint","IMPRINT",FACE,{"disambiguationData":[TD([[makeQuery(id+"F0.imprint","IMPRINT",EDGE,{"derivedFrom":subQ18}),1.0]])]});}
            var Q5;
            Q5=makeQuery(id+"F0.imprint","IMPRINT",FACE,{"disambiguationData":[TD([[makeQuery(id+"F0.imprint","IMPRINT",EDGE,{"derivedFrom":sQuery(id+"F0.wireOp",EDGE,"E8")}),-1.0]])]});
            var Q6;
            {var subQ0=sQuery(id+"F0.wireOp",EDGE,"E16");Q6=makeQuery(id+"F0.imprint","IMPRINT",FACE,{"disambiguationData":[TD([[makeQuery(id+"F0.imprint","IMPRINT",EDGE,{"derivedFrom":subQ0}),1.0]])]});}
            var Q7;
            {var subQ0=sQuery(id+"F0.wireOp",EDGE,"E25");Q7=makeQuery(id+"F0.imprint","IMPRINT",FACE,{"disambiguationData":[TD([[makeQuery(id+"F0.imprint","IMPRINT",EDGE,{"derivedFrom":subQ0}),-1.0]])]});}
            var Q8;
            Q8=makeQuery(id+"F0.imprint","IMPRINT",FACE,{"disambiguationData":[TD([[makeQuery(id+"F0.imprint","IMPRINT",EDGE,{"derivedFrom":sQuery(id+"F0.wireOp",EDGE,"E1")}),-1.0]])]});
            var Q9;
            Q9=makeQuery(id+"F0.imprint","IMPRINT",FACE,{"disambiguationData":[TD([[makeQuery(id+"F0.imprint","IMPRINT",EDGE,{"derivedFrom":sQuery(id+"F0.wireOp",EDGE,"E1")}),1.0]])]});
            var Q10;
            {var subQ0=sQuery(id+"F0.wireOp",EDGE,"E2");var subQ1=sQuery(id+"F0.wireOp",EDGE,"E0");var subQ2=makeQuery(id+"F0.imprint","INTERSECT",VERTEX,{"disambiguationData":[OD(0.0)],"derivedFrom":[subQ1,subQ0]});Q10=makeQuery(id+"F0.imprint","IMPRINT",FACE,{"disambiguationData":[TD([[makeQuery(id+"F0.imprint","IMPRINT",EDGE,{"disambiguationData":[TD([[subQ2,-1.0]])],"derivedFrom":subQ1}),-1.0]])]});}
            var Q11;
            {var subQ0=sQuery(id+"F0.wireOp",EDGE,"E2");var subQ1=sQuery(id+"F0.wireOp",EDGE,"E0");var subQ2=makeQuery(id+"F0.imprint","INTERSECT",VERTEX,{"disambiguationData":[OD(0.0)],"derivedFrom":[subQ1,subQ0]});Q11=makeQuery(id+"F0.imprint","IMPRINT",FACE,{"disambiguationData":[TD([[makeQuery(id+"F0.imprint","IMPRINT",EDGE,{"disambiguationData":[TD([[subQ2,-1.0]])],"derivedFrom":subQ1}),1.0]])]});}
            var Q12;
            {var subQ0=sQuery(id+"F0.wireOp",EDGE,"E29");var subQ1=sQuery(id+"F0.wireOp",EDGE,"E0");var subQ2=makeQuery(id+"F0.imprint","INTERSECT",VERTEX,{"disambiguationData":[OD(0.0)],"derivedFrom":[subQ1,subQ0]});Q12=makeQuery(id+"F0.imprint","IMPRINT",FACE,{"disambiguationData":[TD([[makeQuery(id+"F0.imprint","IMPRINT",EDGE,{"disambiguationData":[TD([[subQ2,-1.0]])],"derivedFrom":subQ1}),1.0]])]});}
            var Q13;
            {var subQ0=sQuery(id+"F0.wireOp",EDGE,"E27");Q13=makeQuery(id+"F0.imprint","IMPRINT",FACE,{"disambiguationData":[TD([[makeQuery(id+"F0.imprint","IMPRINT",EDGE,{"derivedFrom":subQ0}),1.0]])]});}
            var Q14;
            {var subQ0=sQuery(id+"F0.wireOp",EDGE,"E24");Q14=makeQuery(id+"F0.imprint","IMPRINT",FACE,{"disambiguationData":[TD([[makeQuery(id+"F0.imprint","IMPRINT",EDGE,{"derivedFrom":subQ0}),1.0]])]});}
            var Q15;
            {var subQ0=sQuery(id+"F0.wireOp",EDGE,"E13");Q15=makeQuery(id+"F0.imprint","IMPRINT",FACE,{"disambiguationData":[TD([[makeQuery(id+"F0.imprint","IMPRINT",EDGE,{"derivedFrom":subQ0}),1.0]])]});}
            var Q16;
            Q16=makeQuery(id+"F0.imprint","IMPRINT",FACE,{"disambiguationData":[TD([[makeQuery(id+"F0.imprint","IMPRINT",EDGE,{"derivedFrom":sQuery(id+"F0.wireOp",EDGE,"E9")}),-1.0]])]});
            var Q17;
            {var subQ0=sQuery(id+"F0.wireOp",EDGE,"E22");var subQ1=sQuery(id+"F0.wireOp",EDGE,"E6");var subQ2=makeQuery(id+"F0.imprint","INTERSECT",VERTEX,{"derivedFrom":[subQ1,subQ0]});Q17=makeQuery(id+"F0.imprint","IMPRINT",FACE,{"disambiguationData":[TD([[makeQuery(id+"F0.imprint","IMPRINT",EDGE,{"disambiguationData":[TD([[subQ2,1.0]])],"derivedFrom":subQ1}),-1.0]])]});}
            var Q18;
            Q18=makeQuery(id+"F0.imprint","IMPRINT",FACE,{"disambiguationData":[TD([[makeQuery(id+"F0.imprint","IMPRINT",EDGE,{"derivedFrom":sQuery(id+"F0.wireOp",EDGE,"E7")}),-1.0]])]});
            extrude(context, id + "F11", {"entities" : qUnion([Q0, Q1, Q2, Q3, Q4, Q5, Q6, Q7, Q8, Q9, Q10, Q11, Q12, Q13, Q14, Q15, Q16, Q17, Q18]), "oppositeDirection" : true, "depth" : 10 * mm});
        }
        {
            var Q0;
            {var subQ0=sQuery(id+"F0.wireOp",EDGE,"E2");var subQ1=sQuery(id+"F0.wireOp",EDGE,"E0");var subQ2=makeQuery(id+"F0.imprint","INTERSECT",VERTEX,{"disambiguationData":[OD(0.0)],"derivedFrom":[subQ1,subQ0]});Q0=makeQuery(id+"F0.imprint","IMPRINT",FACE,{"disambiguationData":[TD([[makeQuery(id+"F0.imprint","IMPRINT",EDGE,{"disambiguationData":[TD([[subQ2,-1.0]])],"derivedFrom":subQ1}),-1.0]])]});}
            var Q1;
            Q1=makeQuery(id+"F0.imprint","IMPRINT",FACE,{"disambiguationData":[TD([[makeQuery(id+"F0.imprint","IMPRINT",EDGE,{"derivedFrom":sQuery(id+"F0.wireOp",EDGE,"E1")}),1.0]])]});
            var Q2;
            Q2=makeQuery(id+"F0.imprint","IMPRINT",FACE,{"disambiguationData":[TD([[makeQuery(id+"F0.imprint","IMPRINT",EDGE,{"derivedFrom":sQuery(id+"F0.wireOp",EDGE,"E1")}),-1.0]])]});
            var Q3;
            {var subQ0=sQuery(id+"F0.wireOp",EDGE,"E29");var subQ1=sQuery(id+"F0.wireOp",EDGE,"E0");var subQ2=makeQuery(id+"F0.imprint","INTERSECT",VERTEX,{"disambiguationData":[OD(0.0)],"derivedFrom":[subQ1,subQ0]});Q3=makeQuery(id+"F0.imprint","IMPRINT",FACE,{"disambiguationData":[TD([[makeQuery(id+"F0.imprint","IMPRINT",EDGE,{"disambiguationData":[TD([[subQ2,-1.0]])],"derivedFrom":subQ1}),1.0]])]});}
            var Q4;
            {var subQ0=sQuery(id+"F0.wireOp",EDGE,"E2");var subQ1=sQuery(id+"F0.wireOp",EDGE,"E0");var subQ2=makeQuery(id+"F0.imprint","INTERSECT",VERTEX,{"disambiguationData":[OD(0.0)],"derivedFrom":[subQ1,subQ0]});Q4=makeQuery(id+"F0.imprint","IMPRINT",FACE,{"disambiguationData":[TD([[makeQuery(id+"F0.imprint","IMPRINT",EDGE,{"disambiguationData":[TD([[subQ2,-1.0]])],"derivedFrom":subQ1}),1.0]])]});}
            var Q5;
            {var subQ0=sQuery(id+"F0.wireOp",EDGE,"E2");var subQ1=sQuery(id+"F0.wireOp",EDGE,"E0");var subQ2=makeQuery(id+"F0.imprint","INTERSECT",VERTEX,{"disambiguationData":[OD(0.0)],"derivedFrom":[subQ1,subQ0]});Q5=makeQuery(id+"F0.imprint","IMPRINT",FACE,{"disambiguationData":[TD([[makeQuery(id+"F0.imprint","IMPRINT",EDGE,{"disambiguationData":[TD([[subQ2,1.0]])],"derivedFrom":subQ1}),1.0]])]});}
            var Q6;
            {var subQ0=sQuery(id+"F0.wireOp",EDGE,"E3");var subQ1=sQuery(id+"F0.wireOp",EDGE,"E0");var subQ2=makeQuery(id+"F0.imprint","INTERSECT",VERTEX,{"disambiguationData":[OD(0.0)],"derivedFrom":[subQ1,subQ0]});Q6=makeQuery(id+"F0.imprint","IMPRINT",FACE,{"disambiguationData":[TD([[makeQuery(id+"F0.imprint","IMPRINT",EDGE,{"disambiguationData":[TD([[subQ2,1.0]])],"derivedFrom":subQ1}),1.0]])]});}
            extrude(context, id + "F12", {"entities" : qUnion([Q0, Q1, Q2, Q3, Q4, Q5, Q6]), "operationType" : NewBodyOperationType.REMOVE, "oppositeDirection" : true, "depth" : 6 * mm});
        }
        {
            var Q0;
            Q0=makeQuery(id+"F11.opExtrude","CAP_EDGE",EDGE,{"disambiguationData":[OSD([sQuery(id+"F0.wireOp",EDGE,"E14")])],"isStart":false});
            var Q1;
            Q1=makeQuery(id+"F11.opExtrude","CAP_EDGE",EDGE,{"disambiguationData":[OSD([sQuery(id+"F0.wireOp",EDGE,"E17")])],"isStart":false});
            var Q2;
            Q2=makeQuery(id+"F11.opExtrude","CAP_EDGE",EDGE,{"disambiguationData":[OSD([sQuery(id+"F0.wireOp",EDGE,"E12")])],"isStart":false});
            var Q3;
            {var subQ0=sQuery(id+"F0.wireOp",EDGE,"E6");Q3=makeQuery(id+"F11.opExtrude","CAP_EDGE",EDGE,{"disambiguationData":[OSD([subQ0]),TDD([makeQuery(id+"F0.imprint","IMPRINT",EDGE,{"disambiguationData":[TD([[makeQuery(id+"F0.imprint","INTERSECT",VERTEX,{"derivedFrom":[subQ0,sQuery(id+"F0.wireOp",EDGE,"E12")]}),1.0]])],"derivedFrom":subQ0})])],"isStart":false});}
            var Q4;
            Q4=makeQuery(id+"F11.opExtrude","CAP_EDGE",EDGE,{"disambiguationData":[OSD([sQuery(id+"F0.wireOp",EDGE,"E13")])],"isStart":false});
            var Q5;
            Q5=makeQuery(id+"F11.opExtrude","CAP_EDGE",EDGE,{"disambiguationData":[OSD([sQuery(id+"F0.wireOp",EDGE,"E18")])],"isStart":false});
            var Q6;
            Q6=makeQuery(id+"F11.opExtrude","CAP_EDGE",EDGE,{"disambiguationData":[OSD([sQuery(id+"F0.wireOp",EDGE,"E15")])],"isStart":false});
            var Q7;
            Q7=makeQuery(id+"F11.opExtrude","CAP_EDGE",EDGE,{"disambiguationData":[OSD([sQuery(id+"F0.wireOp",EDGE,"E4")])],"isStart":false});
            var Q8;
            Q8=makeQuery(id+"F11.opExtrude","CAP_EDGE",EDGE,{"disambiguationData":[OSD([sQuery(id+"F0.wireOp",EDGE,"E24")])],"isStart":false});
            var Q9;
            Q9=makeQuery(id+"F11.opExtrude","CAP_EDGE",EDGE,{"disambiguationData":[OSD([sQuery(id+"F0.wireOp",EDGE,"E3")])],"isStart":false});
            var Q10;
            Q10=makeQuery(id+"F11.opExtrude","CAP_EDGE",EDGE,{"disambiguationData":[OSD([sQuery(id+"F0.wireOp",EDGE,"E16")])],"isStart":false});
            var Q11;
            Q11=makeQuery(id+"F11.opExtrude","CAP_EDGE",EDGE,{"disambiguationData":[OSD([sQuery(id+"F0.wireOp",EDGE,"E5")])],"isStart":false});
            fillet(context, id + "F13", {"entities" : qUnion([Q0, Q1, Q2, Q3, Q4, Q5, Q6, Q7, Q8, Q9, Q10, Q11]), "radius" : 2 * mm, "tangentPropagation" : true, "allowEdgeOverflow" : false});
        }
        {
            var Q0;
            Q0=makeQuery(id+"F12.boolean.opBoolean","COPY",EDGE,{"derivedFrom":makeQuery(id+"F12.opExtrude","CAP_EDGE",EDGE,{"disambiguationData":[OSD([sQuery(id+"F0.wireOp",EDGE,"E23.trimOffspring")])],"isStart":false})});
            var Q1;
            Q1=makeQuery(id+"F12.boolean.opBoolean","COPY",EDGE,{"derivedFrom":makeQuery(id+"F12.opExtrude","CAP_EDGE",EDGE,{"disambiguationData":[OSD([sQuery(id+"F0.wireOp",EDGE,"E2")])],"isStart":false})});
            var Q2;
            {var subQ0=sQuery(id+"F0.wireOp",EDGE,"E0");Q2=makeQuery(id+"F12.boolean.opBoolean","COPY",EDGE,{"derivedFrom":makeQuery(id+"F12.opExtrude","CAP_EDGE",EDGE,{"disambiguationData":[OSD([subQ0]),TDD([makeQuery(id+"F0.imprint","IMPRINT",EDGE,{"disambiguationData":[TD([[makeQuery(id+"F0.imprint","INTERSECT",VERTEX,{"disambiguationData":[OD(1.0)],"derivedFrom":[subQ0,sQuery(id+"F0.wireOp",EDGE,"E2")]}),-1.0]])],"derivedFrom":subQ0})])],"isStart":false})});}
            var Q3;
            {var subQ0=sQuery(id+"F0.wireOp",EDGE,"E3");Q3=makeQuery(id+"F12.boolean.opBoolean","COPY",EDGE,{"derivedFrom":makeQuery(id+"F12.opExtrude","CAP_EDGE",EDGE,{"disambiguationData":[OSD([subQ0]),TDD([makeQuery(id+"F0.imprint","IMPRINT",EDGE,{"disambiguationData":[TD([[makeQuery(id+"F0.imprint","INTERSECT",VERTEX,{"disambiguationData":[OD(0.0)],"derivedFrom":[subQ0,sQuery(id+"F0.wireOp",EDGE,"E23.trimOffspring")]}),-1.0]])],"derivedFrom":subQ0})])],"isStart":false})});}
            var Q4;
            {var subQ0=sQuery(id+"F0.wireOp",EDGE,"E0");Q4=makeQuery(id+"F12.boolean.opBoolean","COPY",EDGE,{"derivedFrom":makeQuery(id+"F12.opExtrude","CAP_EDGE",EDGE,{"disambiguationData":[OSD([subQ0]),TDD([makeQuery(id+"F0.imprint","IMPRINT",EDGE,{"disambiguationData":[TD([[makeQuery(id+"F0.imprint","INTERSECT",VERTEX,{"disambiguationData":[OD(0.0)],"derivedFrom":[subQ0,sQuery(id+"F0.wireOp",EDGE,"E2")]}),1.0]])],"derivedFrom":subQ0})])],"isStart":false})});}
            var Q5;
            {var subQ0=sQuery(id+"F0.wireOp",EDGE,"E3");Q5=makeQuery(id+"F12.boolean.opBoolean","COPY",EDGE,{"derivedFrom":makeQuery(id+"F12.opExtrude","CAP_EDGE",EDGE,{"disambiguationData":[OSD([subQ0]),TDD([makeQuery(id+"F0.imprint","IMPRINT",EDGE,{"disambiguationData":[TD([[makeQuery(id+"F0.imprint","INTERSECT",VERTEX,{"disambiguationData":[OD(1.0)],"derivedFrom":[subQ0,sQuery(id+"F0.wireOp",EDGE,"E23.trimOffspring")]}),1.0]])],"derivedFrom":subQ0})])],"isStart":false})});}
            fillet(context, id + "F14", {"entities" : qUnion([Q0, Q1, Q2, Q3, Q4, Q5]), "radius" : 2 * mm, "tangentPropagation" : true, "allowEdgeOverflow" : false});
        }
    });
